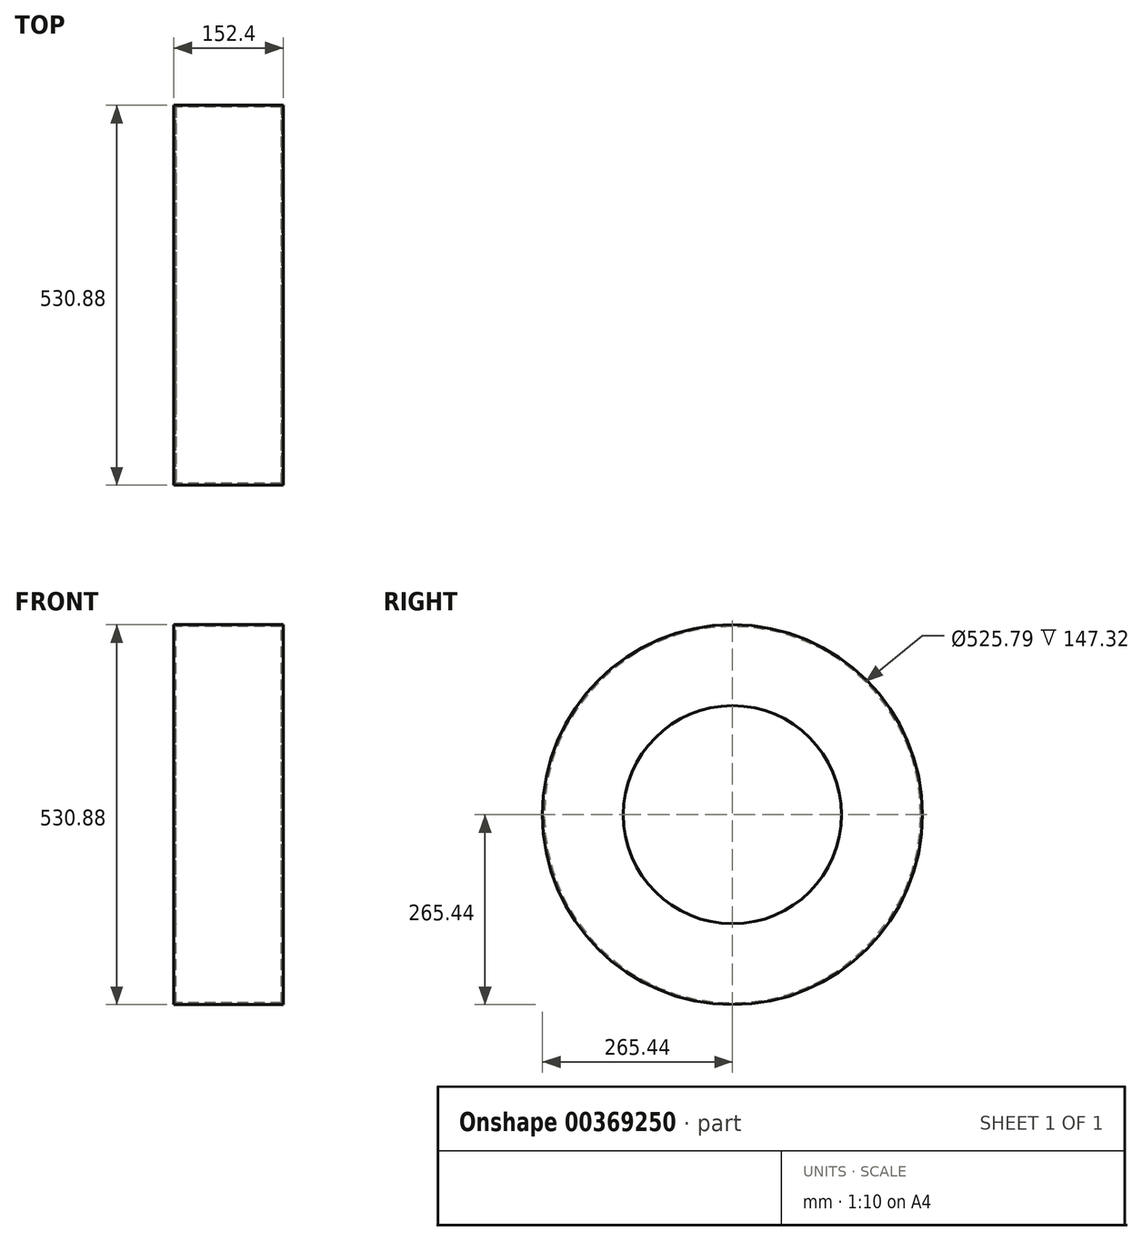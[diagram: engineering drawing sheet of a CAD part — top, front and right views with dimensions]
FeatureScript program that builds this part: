
annotation { "Feature Type Name" : "Feature", "Feature Type Description" : "" }
export const myFeature = defineFeature(function(context is Context, id is Id, definition is map)
    precondition{}
    {
        {
            var Q0;
            Q0=qCreatedBy(makeId("Right.planeOp"),FACE);
            var sketch = newSketch(context, id + "F0", { "sketchPlane" : qUnion([Q0])});
            skCircle(sketch, "E0", {"center": v(0, 0) * mm, "radius": 152.4 * mm});
            skCircle(sketch, "E1", {"center": v(0, 0) * mm, "radius": 265.44 * mm});
            skSolve(sketch);
        }
        {
            var Q0;
            Q0 = qSketchRegion(id + "F0", true);
            extrude(context, id + "F1", {"entities" : qUnion([Q0]), "depth" : 152.4 * mm});
        }
        {
            var Q0;
            Q0=makeQuery(id+"F1.opExtrude","SWEPT_FACE",FACE,{"disambiguationData":[OSD([sQuery(id+"F0.wireOp",EDGE,"E0")])]});
            shell(context, id + "F2", {"entities" : qUnion([Q0]), "thickness" : 2.54 * mm});
        }
        {
            var Q0;
            Q0=makeQuery(id+"F1.opExtrude","CAP_EDGE",EDGE,{"disambiguationData":[OSD([sQuery(id+"F0.wireOp",EDGE,"E0")])],"isStart":false});
            fillet(context, id + "F3", {"entities" : qUnion([Q0]), "radius" : 257.55 * mm, "tangentPropagation" : true, "allowEdgeOverflow" : false});
        }
        {
            var Q0;
            Q0=makeQuery(id+"F1.opExtrude","CAP_EDGE",EDGE,{"disambiguationData":[OSD([sQuery(id+"F0.wireOp",EDGE,"E0")])],"isStart":true});
            fillet(context, id + "F4", {"entities" : qUnion([Q0]), "radius" : 331.13 * mm, "tangentPropagation" : true, "allowEdgeOverflow" : false});
        }
    });
